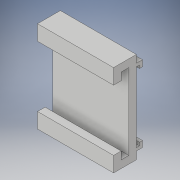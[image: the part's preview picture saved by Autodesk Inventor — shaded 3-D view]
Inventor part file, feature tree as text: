
AUTODESK INVENTOR PART (.ipt)
format: ipt  version: 2019 (Build 230136000, 136)  size: 172,032 bytes
history: native  units: mm
features: sketch x10, extrude x9
ambient origin geometry x8: Origin, YZ Plane, XZ Plane, XY Plane, X Axis, Y Axis, Z Axis, Center Point
bodies: Solid1 (feature_tree)
feature tree (19):
  extrude  "Extrusion1"  Depth=60.0mm
  extrude  "Extrusion2"  Depth=25.0mm
  extrude  "Extrusion3"  Depth=5.0mm
  extrude  "Extrusion4"  Depth=5.0mm
  extrude  "Extrusion5"  Depth=5.0mm
  extrude  "Extrusion6"  Depth=5.0mm
  extrude  "Extrusion7"  Depth=2.0mm
  sketch  "Sketch8"  dims[d19=5.0mm d20=4.0mm d21=0.0mm]
  extrude  "Extrusion8"  Depth=4.0mm TaperAngle=0.0deg
  extrude  "Extrusion9"  Depth=5.0mm
  sketch  "Sketch1"  dims[d0=50.0mm d1=60.0mm]
  sketch  "Sketch2"  dims[d2=30.0mm d3=25.0mm]
  sketch  "Sketch3"  dims[d4=5.0mm d5=0.0mm d6=5.0mm]
  sketch  "Sketch4"  dims[d7=10.0mm d8=0.0mm d9=5.0mm]
  sketch  "Sketch5"  dims[d10=10.0mm d11=0.0mm d12=5.0mm]
  sketch  "Sketch6"  dims[d13=5.0mm d14=0.0mm d15=5.0mm]
  sketch  "Sketch7"  dims[d16=5.0mm d17=0.0mm d18=2.0mm]
  sketch  "Sketch9"  dims[d22=2.0mm d23=5.0mm]
  sketch  "Sketch10"  dims[d24=4.0mm d25=0.0mm d26=2.0mm d27=0.0mm d28=2.0mm d29=0.0mm]
